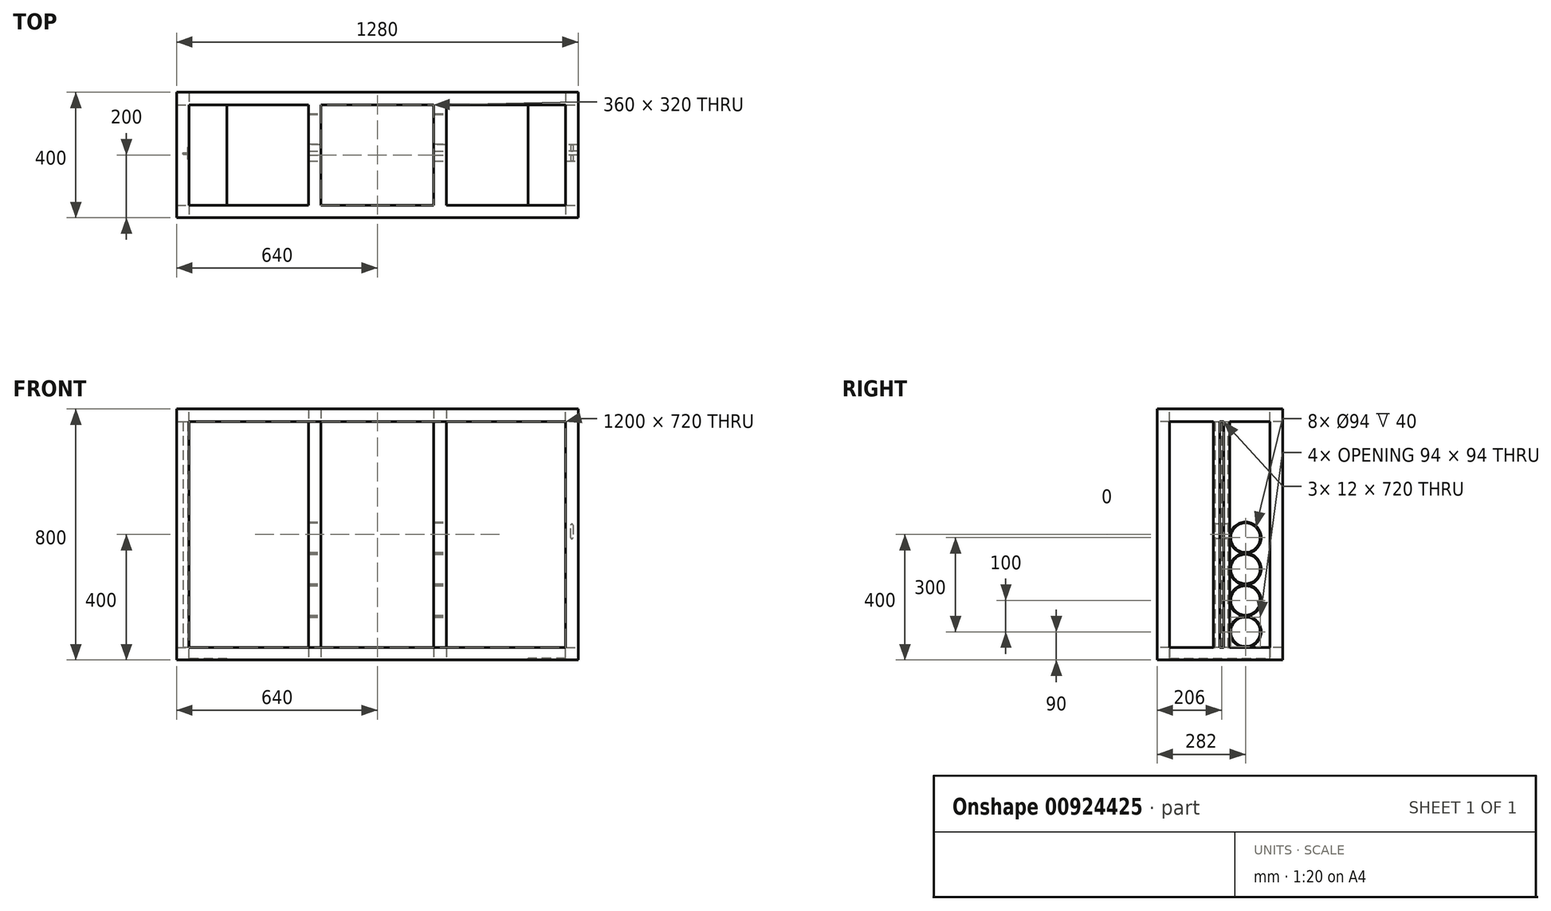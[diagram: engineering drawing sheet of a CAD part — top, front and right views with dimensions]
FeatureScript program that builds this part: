
annotation { "Feature Type Name" : "Feature", "Feature Type Description" : "" }
export const myFeature = defineFeature(function(context is Context, id is Id, definition is map)
    precondition{}
    {
        {
            var Q0;
            Q0=qCreatedBy(makeId("Top.planeOp"),FACE);
            var sketch = newSketch(context, id + "F0", { "sketchPlane" : qUnion([Q0])});
            skLineSegment(sketch, "E0.bottom", {"start": v(0, 0) * mm, "end": v(1280, 0) * mm});
            skLineSegment(sketch, "E0.top", {"start": v(0, 400) * mm, "end": v(1280, 400) * mm});
            skLineSegment(sketch, "E0.left", {"start": v(0, 0) * mm, "end": v(0, 400) * mm});
            skLineSegment(sketch, "E0.right", {"start": v(1280, 0) * mm, "end": v(1280, 400) * mm});
            skSolve(sketch);
        }
        {
            var Q0;
            Q0=makeQuery(id+"F0.imprint","IMPRINT",FACE,{"disambiguationData":[TD([[makeQuery(id+"F0.imprint","IMPRINT",EDGE,{"derivedFrom":sQuery(id+"F0.wireOp",EDGE,"E0.bottom")}),1.0]])]});
            extrude(context, id + "F1", {"entities" : qUnion([Q0]), "depth" : 800 * mm, "offsetDistance" : 25 * mm});
        }
        {
            var Q0;
            Q0=makeQuery(id+"F1.opExtrude","CAP_FACE",FACE,{"disambiguationData":[OSD([sQuery(id+"F0.wireOp",EDGE,"E0.bottom"),sQuery(id+"F0.wireOp",EDGE,"E0.top"),sQuery(id+"F0.wireOp",EDGE,"E0.left"),sQuery(id+"F0.wireOp",EDGE,"E0.right")])],"isStart":false});
            var sketch = newSketch(context, id + "F2", { "sketchPlane" : qUnion([Q0])});
            skLineSegment(sketch, "E1.bottom", {"start": v(40, 40) * mm, "end": v(1240, 40) * mm});
            skLineSegment(sketch, "E1.top", {"start": v(40, 360) * mm, "end": v(1240, 360) * mm});
            skLineSegment(sketch, "E1.left", {"start": v(40, 40) * mm, "end": v(40, 360) * mm});
            skLineSegment(sketch, "E1.right", {"start": v(1240, 40) * mm, "end": v(1240, 360) * mm});
            skSolve(sketch);
        }
        {
            var Q0;
            Q0=makeQuery(id+"F2.imprint","IMPRINT",FACE,{"disambiguationData":[TD([[makeQuery(id+"F2.imprint","IMPRINT",EDGE,{"derivedFrom":sQuery(id+"F2.wireOp",EDGE,"E1.bottom")}),1.0]])]});
            extrude(context, id + "F3", {"entities" : qUnion([Q0]), "operationType" : NewBodyOperationType.REMOVE, "endBound" : BoundingType.THROUGH_ALL, "oppositeDirection" : true, "depth" : 25 * mm, "offsetDistance" : 25 * mm});
        }
        {
            var Q0;
            Q0=makeQuery(id+"F1.opExtrude","SWEPT_FACE",FACE,{"disambiguationData":[OSD([sQuery(id+"F0.wireOp",EDGE,"E0.bottom")])]});
            var sketch = newSketch(context, id + "F4", { "sketchPlane" : qUnion([Q0])});
            skLineSegment(sketch, "E2.bottom", {"start": v(40, 760) * mm, "end": v(1240, 760) * mm});
            skLineSegment(sketch, "E2.top", {"start": v(40, 40) * mm, "end": v(1240, 40) * mm});
            skLineSegment(sketch, "E2.left", {"start": v(40, 760) * mm, "end": v(40, 40) * mm});
            skLineSegment(sketch, "E2.right", {"start": v(1240, 760) * mm, "end": v(1240, 40) * mm});
            skSolve(sketch);
        }
        {
            var Q0;
            Q0=makeQuery(id+"F4.imprint","IMPRINT",FACE,{"disambiguationData":[TD([[makeQuery(id+"F4.imprint","IMPRINT",EDGE,{"derivedFrom":sQuery(id+"F4.wireOp",EDGE,"E2.bottom")}),-1.0]])]});
            extrude(context, id + "F5", {"entities" : qUnion([Q0]), "operationType" : NewBodyOperationType.REMOVE, "endBound" : BoundingType.THROUGH_ALL, "oppositeDirection" : true, "depth" : 25 * mm, "offsetDistance" : 25 * mm});
        }
        {
            var Q0;
            Q0=makeQuery(id+"F1.opExtrude","SWEPT_FACE",FACE,{"disambiguationData":[OSD([sQuery(id+"F0.wireOp",EDGE,"E0.right")])]});
            var sketch = newSketch(context, id + "F6", { "sketchPlane" : qUnion([Q0])});
            skLineSegment(sketch, "E3.bottom", {"start": v(40, 760) * mm, "end": v(360, 760) * mm});
            skLineSegment(sketch, "E3.top", {"start": v(40, 40) * mm, "end": v(360, 40) * mm});
            skLineSegment(sketch, "E3.left", {"start": v(40, 760) * mm, "end": v(40, 40) * mm});
            skLineSegment(sketch, "E3.right", {"start": v(360, 760) * mm, "end": v(360, 40) * mm});
            skSolve(sketch);
        }
        {
            var Q0;
            Q0=makeQuery(id+"F6.imprint","IMPRINT",FACE,{"disambiguationData":[TD([[makeQuery(id+"F6.imprint","IMPRINT",EDGE,{"derivedFrom":sQuery(id+"F6.wireOp",EDGE,"E3.bottom")}),-1.0]])]});
            extrude(context, id + "F7", {"entities" : qUnion([Q0]), "operationType" : NewBodyOperationType.REMOVE, "endBound" : BoundingType.THROUGH_ALL, "oppositeDirection" : true, "depth" : 25 * mm, "offsetDistance" : 25 * mm});
        }
        {
            var Q0;
            Q0=makeQuery(id+"F5.boolean.opBoolean","SPLIT",FACE,{"disambiguationData":[TD([makeQuery(id+"F5.opExtrude","SWEPT_FACE",FACE,{"disambiguationData":[OSD([sQuery(id+"F4.wireOp",EDGE,"E2.top")])]})])],"derivedFrom":makeQuery(id+"F3.boolean.opBoolean","COPY",FACE,{"derivedFrom":makeQuery(id+"F3.opExtrude","SWEPT_FACE",FACE,{"disambiguationData":[OSD([sQuery(id+"F2.wireOp",EDGE,"E1.top")])]})})});
            var sketch = newSketch(context, id + "F8", { "sketchPlane" : qUnion([Q0])});
            skLineSegment(sketch, "E4.bottom", {"start": v(420, 40) * mm, "end": v(460, 40) * mm});
            skLineSegment(sketch, "E4.top", {"start": v(420, 0) * mm, "end": v(460, 0) * mm});
            skLineSegment(sketch, "E4.left", {"start": v(420, 40) * mm, "end": v(420, 0) * mm});
            skLineSegment(sketch, "E4.right", {"start": v(460, 40) * mm, "end": v(460, 0) * mm});
            skLineSegment(sketch, "E5.bottom", {"start": v(820, 40) * mm, "end": v(860, 40) * mm});
            skLineSegment(sketch, "E5.top", {"start": v(820, 0) * mm, "end": v(860, 0) * mm});
            skLineSegment(sketch, "E5.left", {"start": v(820, 40) * mm, "end": v(820, 0) * mm});
            skLineSegment(sketch, "E5.right", {"start": v(860, 40) * mm, "end": v(860, 0) * mm});
            skSolve(sketch);
        }
        {
            var Q0;
            Q0=makeQuery(id+"F8.imprint","IMPRINT",FACE,{"disambiguationData":[TD([[makeQuery(id+"F8.imprint","IMPRINT",EDGE,{"derivedFrom":sQuery(id+"F8.wireOp",EDGE,"E4.bottom")}),-1.0]])]});
            var Q1;
            Q1=makeQuery(id+"F8.imprint","IMPRINT",FACE,{"disambiguationData":[TD([[makeQuery(id+"F8.imprint","IMPRINT",EDGE,{"derivedFrom":sQuery(id+"F8.wireOp",EDGE,"E5.bottom")}),-1.0]])]});
            extrude(context, id + "F9", {"entities" : qUnion([Q0, Q1]), "operationType" : NewBodyOperationType.ADD, "endBound" : BoundingType.UP_TO_NEXT, "depth" : 25 * mm, "offsetDistance" : 25 * mm});
        }
        {
            var Q0;
            Q0=makeQuery(id+"F5.boolean.opBoolean","SPLIT",FACE,{"disambiguationData":[TD([makeQuery(id+"F5.opExtrude","SWEPT_FACE",FACE,{"disambiguationData":[OSD([sQuery(id+"F4.wireOp",EDGE,"E2.bottom")])]})])],"derivedFrom":makeQuery(id+"F3.boolean.opBoolean","COPY",FACE,{"derivedFrom":makeQuery(id+"F3.opExtrude","SWEPT_FACE",FACE,{"disambiguationData":[OSD([sQuery(id+"F2.wireOp",EDGE,"E1.top")])]})})});
            var sketch = newSketch(context, id + "F10", { "sketchPlane" : qUnion([Q0])});
            skLineSegment(sketch, "E6.bottom", {"start": v(420, 800) * mm, "end": v(460, 800) * mm});
            skLineSegment(sketch, "E6.top", {"start": v(420, 760) * mm, "end": v(460, 760) * mm});
            skLineSegment(sketch, "E6.left", {"start": v(420, 800) * mm, "end": v(420, 760) * mm});
            skLineSegment(sketch, "E6.right", {"start": v(460, 800) * mm, "end": v(460, 760) * mm});
            skLineSegment(sketch, "E7.bottom", {"start": v(820, 800) * mm, "end": v(860, 800) * mm});
            skLineSegment(sketch, "E7.top", {"start": v(820, 760) * mm, "end": v(860, 760) * mm});
            skLineSegment(sketch, "E7.left", {"start": v(820, 800) * mm, "end": v(820, 760) * mm});
            skLineSegment(sketch, "E7.right", {"start": v(860, 800) * mm, "end": v(860, 760) * mm});
            skSolve(sketch);
        }
        {
            var Q0;
            Q0 = qSketchRegion(id + "F10", true);
            extrude(context, id + "F11", {"entities" : qUnion([Q0]), "operationType" : NewBodyOperationType.ADD, "endBound" : BoundingType.UP_TO_NEXT, "depth" : 25 * mm, "offsetDistance" : 25 * mm});
        }
        {
            var Q0;
            {var subQ4=makeQuery(id+"F5.opExtrude","SWEPT_FACE",FACE,{"disambiguationData":[OSD([sQuery(id+"F4.wireOp",EDGE,"E2.top")])]});Q0=makeQuery(id+"F9.boolean.opBoolean","MERGE",FACE,{"derivedFrom":[makeQuery(id+"F5.boolean.opBoolean","COPY",FACE,{"disambiguationData":[TD([makeQuery(id+"F1.opExtrude","SWEPT_FACE",FACE,{"disambiguationData":[OSD([sQuery(id+"F0.wireOp",EDGE,"E0.bottom")])]})])],"derivedFrom":subQ4}),makeQuery(id+"F5.boolean.opBoolean","COPY",FACE,{"disambiguationData":[TD([makeQuery(id+"F1.opExtrude","SWEPT_FACE",FACE,{"disambiguationData":[OSD([sQuery(id+"F0.wireOp",EDGE,"E0.top")])]})])],"derivedFrom":subQ4}),makeQuery(id+"F9.opExtrude","SWEPT_FACE",FACE,{"disambiguationData":[OSD([sQuery(id+"F8.wireOp",EDGE,"E4.bottom")])]}),makeQuery(id+"F9.opExtrude","SWEPT_FACE",FACE,{"disambiguationData":[OSD([sQuery(id+"F8.wireOp",EDGE,"E5.bottom")])]})]});}
            var sketch = newSketch(context, id + "F12", { "sketchPlane" : qUnion([Q0])});
            skLineSegment(sketch, "E8.bottom", {"start": v(420, 180) * mm, "end": v(460, 180) * mm});
            skLineSegment(sketch, "E8.top", {"start": v(420, 200) * mm, "end": v(460, 200) * mm});
            skLineSegment(sketch, "E8.left", {"start": v(420, 180) * mm, "end": v(420, 200) * mm});
            skLineSegment(sketch, "E8.right", {"start": v(460, 180) * mm, "end": v(460, 200) * mm});
            skLineSegment(sketch, "E9.bottom", {"start": v(420, 212) * mm, "end": v(460, 212) * mm});
            skLineSegment(sketch, "E9.top", {"start": v(420, 232) * mm, "end": v(460, 232) * mm});
            skLineSegment(sketch, "E9.left", {"start": v(420, 212) * mm, "end": v(420, 232) * mm});
            skLineSegment(sketch, "E9.right", {"start": v(460, 212) * mm, "end": v(460, 232) * mm});
            skLineSegment(sketch, "E10.bottom", {"start": v(820, 180) * mm, "end": v(860, 180) * mm});
            skLineSegment(sketch, "E10.top", {"start": v(820, 200) * mm, "end": v(860, 200) * mm});
            skLineSegment(sketch, "E10.left", {"start": v(820, 180) * mm, "end": v(820, 200) * mm});
            skLineSegment(sketch, "E10.right", {"start": v(860, 180) * mm, "end": v(860, 200) * mm});
            skLineSegment(sketch, "E11.bottom", {"start": v(820, 212) * mm, "end": v(860, 212) * mm});
            skLineSegment(sketch, "E11.top", {"start": v(820, 232) * mm, "end": v(860, 232) * mm});
            skLineSegment(sketch, "E11.left", {"start": v(820, 212) * mm, "end": v(820, 232) * mm});
            skLineSegment(sketch, "E11.right", {"start": v(860, 212) * mm, "end": v(860, 232) * mm});
            skLineSegment(sketch, "E12.bottom", {"start": v(40, 225) * mm, "end": v(35.5, 225) * mm});
            skLineSegment(sketch, "E12.top", {"start": v(40, 185) * mm, "end": v(35.5, 185) * mm});
            skLineSegment(sketch, "E12.left", {"start": v(40, 225) * mm, "end": v(40, 185) * mm});
            skLineSegment(sketch, "E12.right", {"start": v(35.5, 225) * mm, "end": v(35.5, 185) * mm});
            skLineSegment(sketch, "E13.bottom", {"start": v(35.5, 207.25) * mm, "end": v(20, 207.25) * mm});
            skLineSegment(sketch, "E13.top", {"start": v(35.5, 202.75) * mm, "end": v(20, 202.75) * mm});
            skLineSegment(sketch, "E13.left", {"start": v(35.5, 207.25) * mm, "end": v(35.5, 202.75) * mm});
            skLineSegment(sketch, "E13.right", {"start": v(20, 207.25) * mm, "end": v(20, 202.75) * mm});
            skSolve(sketch);
        }
        {
            var Q0;
            Q0=makeQuery(id+"F12.imprint","IMPRINT",FACE,{"disambiguationData":[TD([[makeQuery(id+"F12.imprint","IMPRINT",EDGE,{"derivedFrom":sQuery(id+"F12.wireOp",EDGE,"E8.bottom")}),1.0]])]});
            var Q1;
            Q1=makeQuery(id+"F12.imprint","IMPRINT",FACE,{"disambiguationData":[TD([[makeQuery(id+"F12.imprint","IMPRINT",EDGE,{"derivedFrom":sQuery(id+"F12.wireOp",EDGE,"E11.bottom")}),1.0]])]});
            var Q2;
            Q2=makeQuery(id+"F12.imprint","IMPRINT",FACE,{"disambiguationData":[TD([[makeQuery(id+"F12.imprint","IMPRINT",EDGE,{"derivedFrom":sQuery(id+"F12.wireOp",EDGE,"E10.bottom")}),1.0]])]});
            var Q3;
            Q3=makeQuery(id+"F12.imprint","IMPRINT",FACE,{"disambiguationData":[TD([[makeQuery(id+"F12.imprint","IMPRINT",EDGE,{"derivedFrom":sQuery(id+"F12.wireOp",EDGE,"E9.bottom")}),1.0]])]});
            var Q4;
            Q4=makeQuery(id+"F12.imprint","IMPRINT",FACE,{"disambiguationData":[TD([[makeQuery(id+"F12.imprint","IMPRINT",EDGE,{"derivedFrom":sQuery(id+"F12.wireOp",EDGE,"E13.bottom")}),1.0]])]});
            var Q5;
            {var subQ1=sQuery(id+"F12.wireOp",EDGE,"E12.bottom");Q5=makeQuery(id+"F12.imprint","IMPRINT",FACE,{"disambiguationData":[TD([[makeQuery(id+"F12.imprint","IMPRINT",EDGE,{"derivedFrom":subQ1}),1.0]])]});}
            extrude(context, id + "F13", {"entities" : qUnion([Q0, Q1, Q2, Q3, Q4, Q5]), "operationType" : NewBodyOperationType.ADD, "endBound" : BoundingType.UP_TO_NEXT, "depth" : 25 * mm, "offsetDistance" : 25 * mm});
        }
        {
            var Q0;
            Q0=makeQuery(id+"F13.boolean.opBoolean","MERGE",FACE,{"derivedFrom":[makeQuery(id+"F9.opExtrude","SWEPT_FACE",FACE,{"disambiguationData":[OSD([sQuery(id+"F8.wireOp",EDGE,"E5.right")])]}),makeQuery(id+"F11.opExtrude","SWEPT_FACE",FACE,{"disambiguationData":[OSD([sQuery(id+"F10.wireOp",EDGE,"E7.right")])]}),makeQuery(id+"F13.opExtrude","SWEPT_FACE",FACE,{"disambiguationData":[OSD([sQuery(id+"F12.wireOp",EDGE,"E10.right")])]}),makeQuery(id+"F13.opExtrude","SWEPT_FACE",FACE,{"disambiguationData":[OSD([sQuery(id+"F12.wireOp",EDGE,"E11.right")])]})]});
            var sketch = newSketch(context, id + "F14", { "sketchPlane" : qUnion([Q0])});
            skCircle(sketch, "E14", {"center": v(282, 90) * mm, "radius": 50 * mm});
            skPoint(sketch, "E14.first.point", {"position": v(232, 90) * mm});
            skPoint(sketch, "E14.second.point", {"position": v(282, 40) * mm});
            skPoint(sketch, "E14.third.point", {"position": v(305.18, 134.3) * mm});
            skCircle(sketch, "E15", {"center": v(282, 90) * mm, "radius": 47 * mm});
            skCircle(sketch, "E16", {"center": v(282, 190) * mm, "radius": 50 * mm});
            skPoint(sketch, "E16.first.point", {"position": v(232, 190) * mm});
            skPoint(sketch, "E16.second.point", {"position": v(282, 140) * mm});
            skPoint(sketch, "E16.third.point", {"position": v(305.18, 234.3) * mm});
            skCircle(sketch, "E17", {"center": v(282, 190) * mm, "radius": 47 * mm});
            skCircle(sketch, "E18", {"center": v(282, 290) * mm, "radius": 50 * mm});
            skPoint(sketch, "E18.first.point", {"position": v(232, 290) * mm});
            skPoint(sketch, "E18.second.point", {"position": v(282, 240) * mm});
            skPoint(sketch, "E18.third.point", {"position": v(305.18, 334.3) * mm});
            skCircle(sketch, "E19", {"center": v(282, 290) * mm, "radius": 47 * mm});
            skCircle(sketch, "E20", {"center": v(282, 390) * mm, "radius": 50 * mm});
            skPoint(sketch, "E20.first.point", {"position": v(232, 390) * mm});
            skPoint(sketch, "E20.second.point", {"position": v(282, 340) * mm});
            skPoint(sketch, "E20.third.point", {"position": v(305.18, 434.3) * mm});
            skCircle(sketch, "E21", {"center": v(282, 390) * mm, "radius": 47 * mm});
            skSolve(sketch);
        }
        {
            var Q0;
            Q0=makeQuery(id+"F14.imprint","IMPRINT",FACE,{"disambiguationData":[TD([[makeQuery(id+"F14.imprint","IMPRINT",EDGE,{"derivedFrom":sQuery(id+"F14.wireOp",EDGE,"E21")}),-1.0]])]});
            var Q1;
            Q1=makeQuery(id+"F14.imprint","IMPRINT",FACE,{"disambiguationData":[TD([[makeQuery(id+"F14.imprint","IMPRINT",EDGE,{"derivedFrom":sQuery(id+"F14.wireOp",EDGE,"E19")}),-1.0]])]});
            var Q2;
            Q2=makeQuery(id+"F14.imprint","IMPRINT",FACE,{"disambiguationData":[TD([[makeQuery(id+"F14.imprint","IMPRINT",EDGE,{"derivedFrom":sQuery(id+"F14.wireOp",EDGE,"E17")}),-1.0]])]});
            var Q3;
            Q3=makeQuery(id+"F14.imprint","IMPRINT",FACE,{"disambiguationData":[TD([[makeQuery(id+"F14.imprint","IMPRINT",EDGE,{"derivedFrom":sQuery(id+"F14.wireOp",EDGE,"E15")}),-1.0]])]});
            extrude(context, id + "F15", {"entities" : qUnion([Q0, Q1, Q2, Q3]), "operationType" : NewBodyOperationType.ADD, "oppositeDirection" : true, "depth" : 440 * mm, "offsetDistance" : 25 * mm});
        }
        {
            var Q0;
            Q0=makeQuery(id+"F13.opExtrude","SWEPT_FACE",FACE,{"disambiguationData":[OSD([sQuery(id+"F12.wireOp",EDGE,"E8.bottom")])]});
            var sketch = newSketch(context, id + "F16", { "sketchPlane" : qUnion([Q0])});
            skLineSegment(sketch, "E22.bottom", {"start": v(460, 470) * mm, "end": v(820, 470) * mm});
            skLineSegment(sketch, "E22.top", {"start": v(460, 40) * mm, "end": v(820, 40) * mm});
            skLineSegment(sketch, "E22.left", {"start": v(460, 470) * mm, "end": v(460, 40) * mm});
            skLineSegment(sketch, "E22.right", {"start": v(820, 470) * mm, "end": v(820, 40) * mm});
            skSolve(sketch);
        }
        {
            var Q0;
            Q0=makeQuery(id+"F16.imprint","IMPRINT",FACE,{"disambiguationData":[TD([[makeQuery(id+"F16.imprint","IMPRINT",EDGE,{"derivedFrom":sQuery(id+"F16.wireOp",EDGE,"E22.bottom")}),-1.0]])]});
            extrude(context, id + "F17", {"entities" : qUnion([Q0]), "operationType" : NewBodyOperationType.REMOVE, "endBound" : BoundingType.THROUGH_ALL, "oppositeDirection" : true, "depth" : 25 * mm, "offsetDistance" : 25 * mm});
        }
        {
            var Q0;
            {var subQ0=makeQuery(id+"F3.boolean.opBoolean","COPY",FACE,{"derivedFrom":makeQuery(id+"F3.opExtrude","SWEPT_FACE",FACE,{"disambiguationData":[OSD([sQuery(id+"F2.wireOp",EDGE,"E1.left")])]})});var subQ1=makeQuery(id+"F3.boolean.opBoolean","COPY",FACE,{"derivedFrom":makeQuery(id+"F3.opExtrude","SWEPT_FACE",FACE,{"disambiguationData":[OSD([sQuery(id+"F2.wireOp",EDGE,"E1.top")])]})});var subQ10=makeQuery(id+"F5.opExtrude","SWEPT_FACE",FACE,{"disambiguationData":[OSD([sQuery(id+"F4.wireOp",EDGE,"E2.top")])]});Q0=makeQuery(id+"F9.boolean.opBoolean","SPLIT",FACE,{"disambiguationData":[TD([subQ0])],"derivedFrom":makeQuery(id+"F5.boolean.opBoolean","SPLIT",FACE,{"disambiguationData":[TD([subQ10])],"derivedFrom":subQ1})});}
            var sketch = newSketch(context, id + "F18", { "sketchPlane" : qUnion([Q0])});
            skLineSegment(sketch, "E23.bottom", {"start": v(40, 0) * mm, "end": v(160, 0) * mm});
            skLineSegment(sketch, "E23.top", {"start": v(40, 5) * mm, "end": v(160, 5) * mm});
            skLineSegment(sketch, "E23.left", {"start": v(40, 0) * mm, "end": v(40, 5) * mm});
            skLineSegment(sketch, "E23.right", {"start": v(160, 0) * mm, "end": v(160, 5) * mm});
            skLineSegment(sketch, "E24.bottom", {"start": v(1240, 0) * mm, "end": v(1120, 0) * mm});
            skLineSegment(sketch, "E24.top", {"start": v(1240, 5) * mm, "end": v(1120, 5) * mm});
            skLineSegment(sketch, "E24.left", {"start": v(1240, 0) * mm, "end": v(1240, 5) * mm});
            skLineSegment(sketch, "E24.right", {"start": v(1120, 0) * mm, "end": v(1120, 5) * mm});
            skSolve(sketch);
        }
        {
            var Q0;
            Q0=makeQuery(id+"F18.imprint","IMPRINT",FACE,{"disambiguationData":[TD([[makeQuery(id+"F18.imprint","IMPRINT",EDGE,{"derivedFrom":sQuery(id+"F18.wireOp",EDGE,"E23.bottom")}),1.0]])]});
            var Q1;
            Q1=makeQuery(id+"F18.imprint","IMPRINT",FACE,{"disambiguationData":[TD([[makeQuery(id+"F18.imprint","IMPRINT",EDGE,{"derivedFrom":sQuery(id+"F18.wireOp",EDGE,"E24.bottom")}),-1.0]])]});
            extrude(context, id + "F19", {"entities" : qUnion([Q0, Q1]), "operationType" : NewBodyOperationType.ADD, "endBound" : BoundingType.UP_TO_NEXT, "depth" : 25 * mm, "offsetDistance" : 25 * mm});
        }
        {
            var Q0;
            Q0=makeQuery(id+"F7.boolean.opBoolean","COPY",FACE,{"disambiguationData":[TD([makeQuery(id+"F1.opExtrude","SWEPT_FACE",FACE,{"disambiguationData":[OSD([sQuery(id+"F0.wireOp",EDGE,"E0.right")])]})])],"derivedFrom":makeQuery(id+"F7.opExtrude","SWEPT_FACE",FACE,{"disambiguationData":[OSD([sQuery(id+"F6.wireOp",EDGE,"E3.top")])]})});
            var sketch = newSketch(context, id + "F20", { "sketchPlane" : qUnion([Q0])});
            skLineSegment(sketch, "E25.bottom", {"start": v(1240, 232) * mm, "end": v(1280, 232) * mm});
            skLineSegment(sketch, "E25.top", {"start": v(1240, 212) * mm, "end": v(1280, 212) * mm});
            skLineSegment(sketch, "E25.left", {"start": v(1240, 232) * mm, "end": v(1240, 212) * mm});
            skLineSegment(sketch, "E25.right", {"start": v(1280, 232) * mm, "end": v(1280, 212) * mm});
            skLineSegment(sketch, "E26.bottom", {"start": v(1240, 200) * mm, "end": v(1280, 200) * mm});
            skLineSegment(sketch, "E26.top", {"start": v(1240, 180) * mm, "end": v(1280, 180) * mm});
            skLineSegment(sketch, "E26.left", {"start": v(1240, 200) * mm, "end": v(1240, 180) * mm});
            skLineSegment(sketch, "E26.right", {"start": v(1280, 200) * mm, "end": v(1280, 180) * mm});
            skSolve(sketch);
        }
        {
            var Q0;
            Q0=makeQuery(id+"F20.imprint","IMPRINT",FACE,{"disambiguationData":[TD([[makeQuery(id+"F20.imprint","IMPRINT",EDGE,{"derivedFrom":sQuery(id+"F20.wireOp",EDGE,"E26.bottom")}),-1.0]])]});
            var Q1;
            Q1=makeQuery(id+"F20.imprint","IMPRINT",FACE,{"disambiguationData":[TD([[makeQuery(id+"F20.imprint","IMPRINT",EDGE,{"derivedFrom":sQuery(id+"F20.wireOp",EDGE,"E25.bottom")}),-1.0]])]});
            extrude(context, id + "F21", {"entities" : qUnion([Q0, Q1]), "operationType" : NewBodyOperationType.ADD, "endBound" : BoundingType.UP_TO_NEXT, "depth" : 25 * mm, "offsetDistance" : 25 * mm});
        }
        {
            var Q0;
            Q0=makeQuery(id+"F21.opExtrude","SWEPT_FACE",FACE,{"disambiguationData":[OSD([sQuery(id+"F20.wireOp",EDGE,"E26.top")])]});
            var sketch = newSketch(context, id + "F22", { "sketchPlane" : qUnion([Q0])});
            skLineSegment(sketch, "E27", {"start": v(1256.5, 390) * mm, "end": v(1256.5, 430) * mm});
            skLineSegment(sketch, "E28", {"start": v(1263.5, 430) * mm, "end": v(1263.5, 390) * mm});
            skArc(sketch, "E29", {"start": v(1263.5, 430) * mm, "mid": v(1260, 433.5) * mm, "end": v(1256.5, 430) * mm});
            skArc(sketch, "E30", {"start": v(1256.5, 390) * mm, "mid": v(1260, 386.5) * mm, "end": v(1263.5, 390) * mm});
            skSolve(sketch);
        }
        {
            var Q0;
            Q0=makeQuery(id+"F22.imprint","IMPRINT",FACE,{"disambiguationData":[TD([[makeQuery(id+"F22.imprint","IMPRINT",EDGE,{"derivedFrom":sQuery(id+"F22.wireOp",EDGE,"E27")}),-1.0]])]});
            var Q1;
            Q1=makeQuery(id+"F21.opExtrude","SWEPT_FACE",FACE,{"disambiguationData":[OSD([sQuery(id+"F20.wireOp",EDGE,"E25.bottom")])]});
            extrude(context, id + "F23", {"entities" : qUnion([Q0]), "operationType" : NewBodyOperationType.REMOVE, "endBound" : BoundingType.UP_TO_SURFACE, "oppositeDirection" : true, "depth" : 25 * mm, "endBoundEntityFace" : qUnion([Q1]), "offsetDistance" : 25 * mm});
        }
    });
